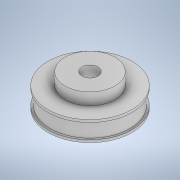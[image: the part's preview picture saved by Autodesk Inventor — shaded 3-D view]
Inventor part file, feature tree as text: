
AUTODESK INVENTOR PART (.ipt)
format: ipt  version: 2021 (Build 250183000, 183)  size: 134,144 bytes
history: native  units: mm
features: extrude x3, sketch x3, plane x1
ambient origin geometry x8: Origin, YZ Plane, XZ Plane, XY Plane, X Axis, Y Axis, Z Axis, Center Point
bodies: Solid1 (feature_tree)
feature tree (7):
  extrude  "Extrusion1"  Depth=8.0mm
  extrude  "Extrusion2"  Depth=10.0mm
  plane  "Work Plane1"
  extrude  "Extrusion3"  Depth=6.0mm TaperAngle=0.0deg
  sketch  "Sketch1"  dims[d0=42.0mm d1=8.0mm]
  sketch  "Sketch2"  dims[d2=10.0mm d3=0.0mm d4=8.0mm]
  sketch  "Sketch3"  dims[d5=25.0mm d6=6.0mm d7=0.0mm d8=-1.25mm d9=1.0mm d10=7.5mm d11=0.0mm]
